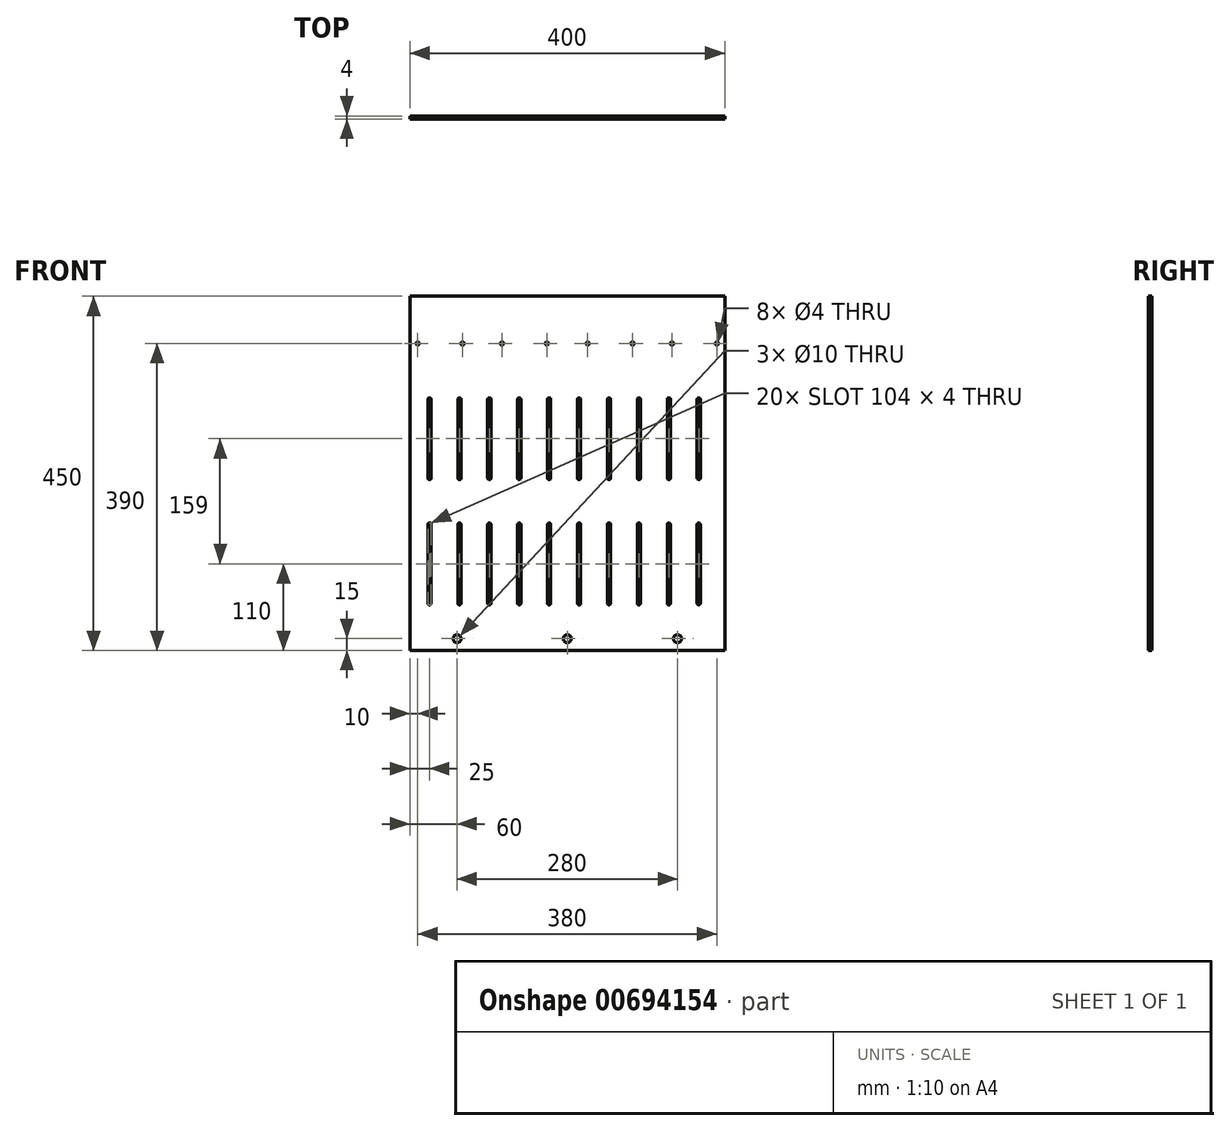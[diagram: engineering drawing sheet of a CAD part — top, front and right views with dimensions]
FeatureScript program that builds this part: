
annotation { "Feature Type Name" : "Feature", "Feature Type Description" : "" }
export const myFeature = defineFeature(function(context is Context, id is Id, definition is map)
    precondition{}
    {
        {
            var Q0;
            Q0=qCreatedBy(makeId("Front.planeOp"),FACE);
            var sketch = newSketch(context, id + "F0", { "sketchPlane" : qUnion([Q0])});
            skLineSegment(sketch, "E0.bottom", {"start": v(-200, -225) * mm, "end": v(200, -225) * mm});
            skLineSegment(sketch, "E0.top", {"start": v(-200, 225) * mm, "end": v(200, 225) * mm});
            skLineSegment(sketch, "E0.left", {"start": v(-200, -225) * mm, "end": v(-200, 225) * mm});
            skLineSegment(sketch, "E0.right", {"start": v(200, -225) * mm, "end": v(200, 225) * mm});
            skPoint(sketch, "E0.middle", {"position": v(0, 0) * mm});
            skCircle(sketch, "E1", {"center": v(-190, 165) * mm, "radius": 2 * mm});
            skCircle(sketch, "E2", {"center": v(-133, 165) * mm, "radius": 2 * mm});
            skCircle(sketch, "E3", {"center": v(-83, 165) * mm, "radius": 2 * mm});
            skCircle(sketch, "E4", {"center": v(-26, 165) * mm, "radius": 2 * mm});
            skCircle(sketch, "E5", {"center": v(26, 165) * mm, "radius": 2 * mm});
            skCircle(sketch, "E6", {"center": v(83, 165) * mm, "radius": 2 * mm});
            skCircle(sketch, "E7", {"center": v(133, 165) * mm, "radius": 2 * mm});
            skCircle(sketch, "E8", {"center": v(190, 165) * mm, "radius": 2 * mm});
            skSolve(sketch);
        }
        {
            var Q0;
            Q0 = qSketchRegion(id + "F0", true);
            extrude(context, id + "F1", {"entities" : qUnion([Q0]), "depth" : 4 * mm, "offsetDistance" : 25 * mm});
        }
        {
            var Q0;
            Q0=makeQuery(id+"F1.opExtrude","CAP_FACE",FACE,{"disambiguationData":[OSD([sQuery(id+"F0.wireOp",EDGE,"E0.bottom"),sQuery(id+"F0.wireOp",EDGE,"E0.top"),sQuery(id+"F0.wireOp",EDGE,"E0.left"),sQuery(id+"F0.wireOp",EDGE,"E0.right"),sQuery(id+"F0.wireOp",EDGE,"E1"),sQuery(id+"F0.wireOp",EDGE,"E2"),sQuery(id+"F0.wireOp",EDGE,"E3"),sQuery(id+"F0.wireOp",EDGE,"E4"),sQuery(id+"F0.wireOp",EDGE,"E5"),sQuery(id+"F0.wireOp",EDGE,"E6"),sQuery(id+"F0.wireOp",EDGE,"E7"),sQuery(id+"F0.wireOp",EDGE,"E8")])],"isStart":true});
            var sketch = newSketch(context, id + "F2", { "sketchPlane" : qUnion([Q0])});
            skCircle(sketch, "E9", {"center": v(0, -210) * mm, "radius": 5 * mm});
            skPoint(sketch, "E9.centerSnap0", {"position": v(0, -225) * mm});
            skCircle(sketch, "E10", {"center": v(140, -210) * mm, "radius": 5 * mm});
            skCircle(sketch, "E11", {"center": v(-140, -210) * mm, "radius": 5 * mm});
            skSolve(sketch);
        }
        {
            var Q0;
            Q0 = qSketchRegion(id + "F2", true);
            extrude(context, id + "F3", {"entities" : qUnion([Q0]), "operationType" : NewBodyOperationType.REMOVE, "oppositeDirection" : true, "depth" : 25 * mm, "offsetDistance" : 25 * mm});
        }
        {
            var Q0;
            Q0=makeQuery(id+"F1.opExtrude","CAP_FACE",FACE,{"disambiguationData":[OSD([sQuery(id+"F0.wireOp",EDGE,"E0.bottom"),sQuery(id+"F0.wireOp",EDGE,"E0.top"),sQuery(id+"F0.wireOp",EDGE,"E0.left"),sQuery(id+"F0.wireOp",EDGE,"E0.right"),sQuery(id+"F0.wireOp",EDGE,"E1"),sQuery(id+"F0.wireOp",EDGE,"E2"),sQuery(id+"F0.wireOp",EDGE,"E3"),sQuery(id+"F0.wireOp",EDGE,"E4"),sQuery(id+"F0.wireOp",EDGE,"E5"),sQuery(id+"F0.wireOp",EDGE,"E6"),sQuery(id+"F0.wireOp",EDGE,"E7"),sQuery(id+"F0.wireOp",EDGE,"E8")])],"isStart":true});
            var sketch = newSketch(context, id + "F4", { "sketchPlane" : qUnion([Q0])});
            skLineSegment(sketch, "E12.left", {"start": v(177, -165) * mm, "end": v(177, -65) * mm});
            skLineSegment(sketch, "E12.right", {"start": v(173, -165) * mm, "end": v(173, -65) * mm});
            skArc(sketch, "E13", {"start": v(173, -165) * mm, "mid": v(175, -167) * mm, "end": v(177, -165) * mm});
            skArc(sketch, "E14", {"start": v(177, -65) * mm, "mid": v(175, -63) * mm, "end": v(173, -65) * mm});
            skArc(sketch, "E15.0.1.0", {"start": v(173, -6) * mm, "mid": v(175, -8) * mm, "end": v(177, -6) * mm});
            skLineSegment(sketch, "E15.0.1.1", {"start": v(173, -6) * mm, "end": v(173, 94) * mm});
            skLineSegment(sketch, "E15.0.1.2", {"start": v(177, -6) * mm, "end": v(177, 94) * mm});
            skArc(sketch, "E15.0.1.3", {"start": v(177, 94) * mm, "mid": v(175, 96) * mm, "end": v(173, 94) * mm});
            skArc(sketch, "E15.1.0.0", {"start": v(135, -165) * mm, "mid": v(137, -167) * mm, "end": v(139, -165) * mm});
            skLineSegment(sketch, "E15.1.0.1", {"start": v(135, -165) * mm, "end": v(135, -65) * mm});
            skLineSegment(sketch, "E15.1.0.2", {"start": v(139, -165) * mm, "end": v(139, -65) * mm});
            skArc(sketch, "E15.1.0.3", {"start": v(139, -65) * mm, "mid": v(137, -63) * mm, "end": v(135, -65) * mm});
            skArc(sketch, "E15.1.1.0", {"start": v(135, -6) * mm, "mid": v(137, -8) * mm, "end": v(139, -6) * mm});
            skLineSegment(sketch, "E15.1.1.1", {"start": v(135, -6) * mm, "end": v(135, 94) * mm});
            skLineSegment(sketch, "E15.1.1.2", {"start": v(139, -6) * mm, "end": v(139, 94) * mm});
            skArc(sketch, "E15.1.1.3", {"start": v(139, 94) * mm, "mid": v(137, 96) * mm, "end": v(135, 94) * mm});
            skArc(sketch, "E15.2.0.0", {"start": v(97, -165) * mm, "mid": v(99, -167) * mm, "end": v(101, -165) * mm});
            skLineSegment(sketch, "E15.2.0.1", {"start": v(97, -165) * mm, "end": v(97, -65) * mm});
            skLineSegment(sketch, "E15.2.0.2", {"start": v(101, -165) * mm, "end": v(101, -65) * mm});
            skArc(sketch, "E15.2.0.3", {"start": v(101, -65) * mm, "mid": v(99, -63) * mm, "end": v(97, -65) * mm});
            skArc(sketch, "E15.2.1.0", {"start": v(97, -6) * mm, "mid": v(99, -8) * mm, "end": v(101, -6) * mm});
            skLineSegment(sketch, "E15.2.1.1", {"start": v(97, -6) * mm, "end": v(97, 94) * mm});
            skLineSegment(sketch, "E15.2.1.2", {"start": v(101, -6) * mm, "end": v(101, 94) * mm});
            skArc(sketch, "E15.2.1.3", {"start": v(101, 94) * mm, "mid": v(99, 96) * mm, "end": v(97, 94) * mm});
            skArc(sketch, "E15.3.0.0", {"start": v(59, -165) * mm, "mid": v(61, -167) * mm, "end": v(63, -165) * mm});
            skLineSegment(sketch, "E15.3.0.1", {"start": v(59, -165) * mm, "end": v(59, -65) * mm});
            skLineSegment(sketch, "E15.3.0.2", {"start": v(63, -165) * mm, "end": v(63, -65) * mm});
            skArc(sketch, "E15.3.0.3", {"start": v(63, -65) * mm, "mid": v(61, -63) * mm, "end": v(59, -65) * mm});
            skArc(sketch, "E15.3.1.0", {"start": v(59, -6) * mm, "mid": v(61, -8) * mm, "end": v(63, -6) * mm});
            skLineSegment(sketch, "E15.3.1.1", {"start": v(59, -6) * mm, "end": v(59, 94) * mm});
            skLineSegment(sketch, "E15.3.1.2", {"start": v(63, -6) * mm, "end": v(63, 94) * mm});
            skArc(sketch, "E15.3.1.3", {"start": v(63, 94) * mm, "mid": v(61, 96) * mm, "end": v(59, 94) * mm});
            skArc(sketch, "E15.4.0.0", {"start": v(21, -165) * mm, "mid": v(23, -167) * mm, "end": v(25, -165) * mm});
            skLineSegment(sketch, "E15.4.0.1", {"start": v(21, -165) * mm, "end": v(21, -65) * mm});
            skLineSegment(sketch, "E15.4.0.2", {"start": v(25, -165) * mm, "end": v(25, -65) * mm});
            skArc(sketch, "E15.4.0.3", {"start": v(25, -65) * mm, "mid": v(23, -63) * mm, "end": v(21, -65) * mm});
            skArc(sketch, "E15.4.1.0", {"start": v(21, -6) * mm, "mid": v(23, -8) * mm, "end": v(25, -6) * mm});
            skLineSegment(sketch, "E15.4.1.1", {"start": v(21, -6) * mm, "end": v(21, 94) * mm});
            skLineSegment(sketch, "E15.4.1.2", {"start": v(25, -6) * mm, "end": v(25, 94) * mm});
            skArc(sketch, "E15.4.1.3", {"start": v(25, 94) * mm, "mid": v(23, 96) * mm, "end": v(21, 94) * mm});
            skArc(sketch, "E15.5.0.0", {"start": v(-17, -165) * mm, "mid": v(-15, -167) * mm, "end": v(-13, -165) * mm});
            skLineSegment(sketch, "E15.5.0.1", {"start": v(-17, -165) * mm, "end": v(-17, -65) * mm});
            skLineSegment(sketch, "E15.5.0.2", {"start": v(-13, -165) * mm, "end": v(-13, -65) * mm});
            skArc(sketch, "E15.5.0.3", {"start": v(-13, -65) * mm, "mid": v(-15, -63) * mm, "end": v(-17, -65) * mm});
            skArc(sketch, "E15.5.1.0", {"start": v(-17, -6) * mm, "mid": v(-15, -8) * mm, "end": v(-13, -6) * mm});
            skLineSegment(sketch, "E15.5.1.1", {"start": v(-17, -6) * mm, "end": v(-17, 94) * mm});
            skLineSegment(sketch, "E15.5.1.2", {"start": v(-13, -6) * mm, "end": v(-13, 94) * mm});
            skArc(sketch, "E15.5.1.3", {"start": v(-13, 94) * mm, "mid": v(-15, 96) * mm, "end": v(-17, 94) * mm});
            skArc(sketch, "E15.6.0.0", {"start": v(-55, -165) * mm, "mid": v(-53, -167) * mm, "end": v(-51, -165) * mm});
            skLineSegment(sketch, "E15.6.0.1", {"start": v(-55, -165) * mm, "end": v(-55, -65) * mm});
            skLineSegment(sketch, "E15.6.0.2", {"start": v(-51, -165) * mm, "end": v(-51, -65) * mm});
            skArc(sketch, "E15.6.0.3", {"start": v(-51, -65) * mm, "mid": v(-53, -63) * mm, "end": v(-55, -65) * mm});
            skArc(sketch, "E15.6.1.0", {"start": v(-55, -6) * mm, "mid": v(-53, -8) * mm, "end": v(-51, -6) * mm});
            skLineSegment(sketch, "E15.6.1.1", {"start": v(-55, -6) * mm, "end": v(-55, 94) * mm});
            skLineSegment(sketch, "E15.6.1.2", {"start": v(-51, -6) * mm, "end": v(-51, 94) * mm});
            skArc(sketch, "E15.6.1.3", {"start": v(-51, 94) * mm, "mid": v(-53, 96) * mm, "end": v(-55, 94) * mm});
            skArc(sketch, "E15.7.0.0", {"start": v(-93, -165) * mm, "mid": v(-91, -167) * mm, "end": v(-89, -165) * mm});
            skLineSegment(sketch, "E15.7.0.1", {"start": v(-93, -165) * mm, "end": v(-93, -65) * mm});
            skLineSegment(sketch, "E15.7.0.2", {"start": v(-89, -165) * mm, "end": v(-89, -65) * mm});
            skArc(sketch, "E15.7.0.3", {"start": v(-89, -65) * mm, "mid": v(-91, -63) * mm, "end": v(-93, -65) * mm});
            skArc(sketch, "E15.7.1.0", {"start": v(-93, -6) * mm, "mid": v(-91, -8) * mm, "end": v(-89, -6) * mm});
            skLineSegment(sketch, "E15.7.1.1", {"start": v(-93, -6) * mm, "end": v(-93, 94) * mm});
            skLineSegment(sketch, "E15.7.1.2", {"start": v(-89, -6) * mm, "end": v(-89, 94) * mm});
            skArc(sketch, "E15.7.1.3", {"start": v(-89, 94) * mm, "mid": v(-91, 96) * mm, "end": v(-93, 94) * mm});
            skArc(sketch, "E15.8.0.0", {"start": v(-131, -165) * mm, "mid": v(-129, -167) * mm, "end": v(-127, -165) * mm});
            skLineSegment(sketch, "E15.8.0.1", {"start": v(-131, -165) * mm, "end": v(-131, -65) * mm});
            skLineSegment(sketch, "E15.8.0.2", {"start": v(-127, -165) * mm, "end": v(-127, -65) * mm});
            skArc(sketch, "E15.8.0.3", {"start": v(-127, -65) * mm, "mid": v(-129, -63) * mm, "end": v(-131, -65) * mm});
            skArc(sketch, "E15.8.1.0", {"start": v(-131, -6) * mm, "mid": v(-129, -8) * mm, "end": v(-127, -6) * mm});
            skLineSegment(sketch, "E15.8.1.1", {"start": v(-131, -6) * mm, "end": v(-131, 94) * mm});
            skLineSegment(sketch, "E15.8.1.2", {"start": v(-127, -6) * mm, "end": v(-127, 94) * mm});
            skArc(sketch, "E15.8.1.3", {"start": v(-127, 94) * mm, "mid": v(-129, 96) * mm, "end": v(-131, 94) * mm});
            skArc(sketch, "E15.9.0.0", {"start": v(-169, -165) * mm, "mid": v(-167, -167) * mm, "end": v(-165, -165) * mm});
            skLineSegment(sketch, "E15.9.0.1", {"start": v(-169, -165) * mm, "end": v(-169, -65) * mm});
            skLineSegment(sketch, "E15.9.0.2", {"start": v(-165, -165) * mm, "end": v(-165, -65) * mm});
            skArc(sketch, "E15.9.0.3", {"start": v(-165, -65) * mm, "mid": v(-167, -63) * mm, "end": v(-169, -65) * mm});
            skArc(sketch, "E15.9.1.0", {"start": v(-169, -6) * mm, "mid": v(-167, -8) * mm, "end": v(-165, -6) * mm});
            skLineSegment(sketch, "E15.9.1.1", {"start": v(-169, -6) * mm, "end": v(-169, 94) * mm});
            skLineSegment(sketch, "E15.9.1.2", {"start": v(-165, -6) * mm, "end": v(-165, 94) * mm});
            skArc(sketch, "E15.9.1.3", {"start": v(-165, 94) * mm, "mid": v(-167, 96) * mm, "end": v(-169, 94) * mm});
            skLineSegment(sketch, "E15.direction1", {"start": v(173, -165) * mm, "end": v(135, -165) * mm, "construction": true});
            skLineSegment(sketch, "E15.direction2", {"start": v(173, -165) * mm, "end": v(173, -6) * mm, "construction": true});
            skSolve(sketch);
        }
        {
            var Q0;
            Q0 = qSketchRegion(id + "F4", true);
            extrude(context, id + "F5", {"entities" : qUnion([Q0]), "operationType" : NewBodyOperationType.REMOVE, "oppositeDirection" : true, "depth" : 25 * mm, "offsetDistance" : 25 * mm});
        }
    });
